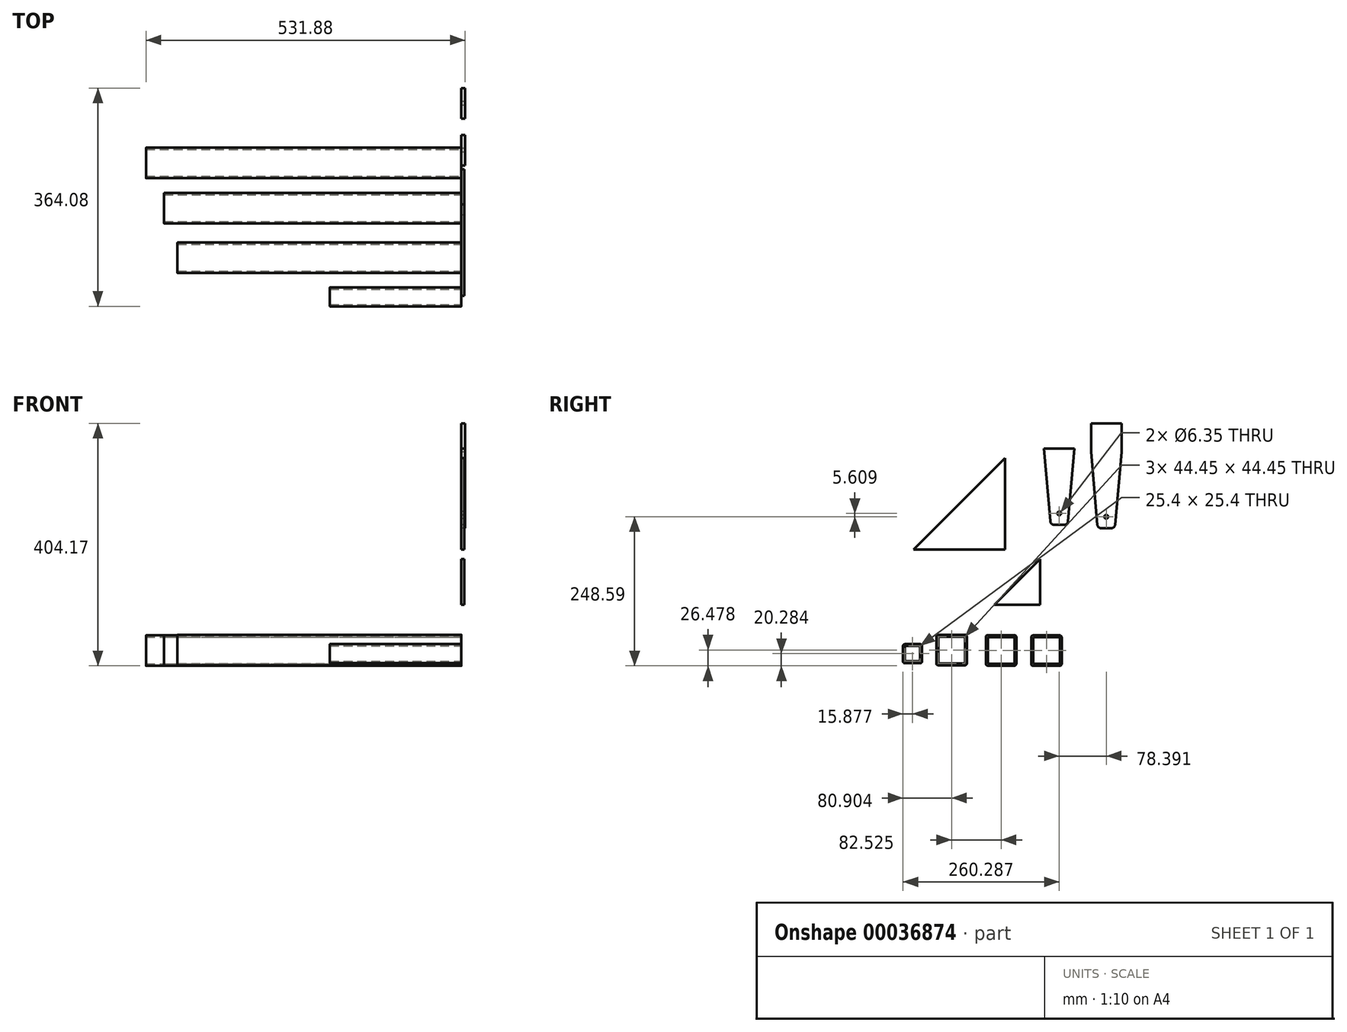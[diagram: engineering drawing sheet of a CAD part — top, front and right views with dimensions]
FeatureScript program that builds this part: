
annotation { "Feature Type Name" : "Feature", "Feature Type Description" : "" }
export const myFeature = defineFeature(function(context is Context, id is Id, definition is map)
    precondition{}
    {
        {
            var Q0;
            Q0=qCreatedBy(makeId("Right.planeOp"),FACE);
            var sketch = newSketch(context, id + "F0", { "sketchPlane" : qUnion([Q0])});
            skLineSegment(sketch, "E0.rect.bottom", {"start": v(22.23, 25.4) * mm, "end": v(-22.23, 25.4) * mm});
            skLineSegment(sketch, "E0.rect.top", {"start": v(22.23, -25.4) * mm, "end": v(-22.23, -25.4) * mm});
            skLineSegment(sketch, "E0.rect.left", {"start": v(25.4, 22.22) * mm, "end": v(25.4, -22.23) * mm});
            skLineSegment(sketch, "E0.rect.right", {"start": v(-25.4, 22.23) * mm, "end": v(-25.4, -22.22) * mm});
            skPoint(sketch, "E0.rect.middle", {"position": v(0, 0) * mm});
            skPoint(sketch, "E1.visualSharp", {"position": v(-25.4, 25.4) * mm});
            skArc(sketch, "E1.filletArc", {"start": v(-22.23, 25.4) * mm, "mid": v(-24.47, 24.47) * mm, "end": v(-25.4, 22.23) * mm});
            skPoint(sketch, "E2.visualSharp", {"position": v(25.4, 25.4) * mm});
            skArc(sketch, "E2.filletArc", {"start": v(25.4, 22.22) * mm, "mid": v(24.47, 24.47) * mm, "end": v(22.23, 25.4) * mm});
            skPoint(sketch, "E3.visualSharp", {"position": v(25.4, -25.4) * mm});
            skArc(sketch, "E3.filletArc", {"start": v(22.23, -25.4) * mm, "mid": v(24.47, -24.47) * mm, "end": v(25.4, -22.23) * mm});
            skPoint(sketch, "E4.visualSharp", {"position": v(-25.4, -25.4) * mm});
            skArc(sketch, "E4.filletArc", {"start": v(-25.4, -22.22) * mm, "mid": v(-24.47, -24.47) * mm, "end": v(-22.23, -25.4) * mm});
            skLineSegment(sketch, "E5.bottom", {"start": v(-22.23, 22.23) * mm, "end": v(22.22, 22.23) * mm});
            skLineSegment(sketch, "E5.top", {"start": v(-22.23, -22.23) * mm, "end": v(22.22, -22.23) * mm});
            skLineSegment(sketch, "E5.left", {"start": v(-22.23, 22.23) * mm, "end": v(-22.23, -22.23) * mm});
            skLineSegment(sketch, "E5.right", {"start": v(22.22, 22.23) * mm, "end": v(22.22, -22.23) * mm});
            skSolve(sketch);
        }
        {
            var Q0;
            Q0=qCreatedBy(makeId("Right.planeOp"),FACE);
            var sketch = newSketch(context, id + "F1", { "sketchPlane" : qUnion([Q0])});
            skLineSegment(sketch, "E6.rect.bottom", {"start": v(-61.4, 48.87) * mm, "end": v(-105.85, 48.87) * mm});
            skLineSegment(sketch, "E6.rect.top", {"start": v(-61.4, -1.93) * mm, "end": v(-105.85, -1.93) * mm});
            skLineSegment(sketch, "E6.rect.left", {"start": v(-58.23, 45.7) * mm, "end": v(-58.23, 1.24) * mm});
            skLineSegment(sketch, "E6.rect.right", {"start": v(-109.03, 45.7) * mm, "end": v(-109.03, 1.24) * mm});
            skPoint(sketch, "E6.rect.middle", {"position": v(-83.63, 23.47) * mm});
            skPoint(sketch, "E7.visualSharp", {"position": v(-109.03, 48.87) * mm});
            skArc(sketch, "E7.filletArc", {"start": v(-105.85, 48.87) * mm, "mid": v(-108.1, 47.94) * mm, "end": v(-109.03, 45.7) * mm});
            skPoint(sketch, "E8.visualSharp", {"position": v(-58.23, 48.87) * mm});
            skArc(sketch, "E8.filletArc", {"start": v(-58.23, 45.7) * mm, "mid": v(-59.16, 47.94) * mm, "end": v(-61.4, 48.87) * mm});
            skPoint(sketch, "E9.visualSharp", {"position": v(-58.23, -1.93) * mm});
            skArc(sketch, "E9.filletArc", {"start": v(-61.4, -1.93) * mm, "mid": v(-59.16, -1) * mm, "end": v(-58.23, 1.24) * mm});
            skPoint(sketch, "E10.visualSharp", {"position": v(-109.03, -1.93) * mm});
            skArc(sketch, "E10.filletArc", {"start": v(-109.03, 1.24) * mm, "mid": v(-108.1, -1) * mm, "end": v(-105.85, -1.93) * mm});
            skLineSegment(sketch, "E11.bottom", {"start": v(-105.85, 45.7) * mm, "end": v(-61.4, 45.7) * mm});
            skLineSegment(sketch, "E11.top", {"start": v(-105.85, 1.24) * mm, "end": v(-61.4, 1.24) * mm});
            skLineSegment(sketch, "E11.left", {"start": v(-105.85, 45.7) * mm, "end": v(-105.85, 1.24) * mm});
            skLineSegment(sketch, "E11.right", {"start": v(-61.4, 45.7) * mm, "end": v(-61.4, 1.24) * mm});
            skSolve(sketch);
        }
        {
            var Q0;
            Q0=qCreatedBy(makeId("Right.planeOp"),FACE);
            var sketch = newSketch(context, id + "F2", { "sketchPlane" : qUnion([Q0])});
            skLineSegment(sketch, "E12.rect.bottom", {"start": v(70.63, 77.05) * mm, "end": v(26.18, 77.05) * mm});
            skLineSegment(sketch, "E12.rect.top", {"start": v(70.63, 26.25) * mm, "end": v(26.18, 26.25) * mm});
            skLineSegment(sketch, "E12.rect.left", {"start": v(73.8, 73.88) * mm, "end": v(73.8, 29.43) * mm});
            skLineSegment(sketch, "E12.rect.right", {"start": v(23, 73.88) * mm, "end": v(23, 29.43) * mm});
            skPoint(sketch, "E12.rect.middle", {"position": v(48.4, 51.65) * mm});
            skPoint(sketch, "E13.visualSharp", {"position": v(23, 77.05) * mm});
            skArc(sketch, "E13.filletArc", {"start": v(26.18, 77.05) * mm, "mid": v(23.94, 76.12) * mm, "end": v(23, 73.88) * mm});
            skPoint(sketch, "E14.visualSharp", {"position": v(73.8, 77.05) * mm});
            skArc(sketch, "E14.filletArc", {"start": v(73.8, 73.88) * mm, "mid": v(72.88, 76.12) * mm, "end": v(70.63, 77.05) * mm});
            skPoint(sketch, "E15.visualSharp", {"position": v(73.8, 26.25) * mm});
            skArc(sketch, "E15.filletArc", {"start": v(70.63, 26.25) * mm, "mid": v(72.88, 27.18) * mm, "end": v(73.8, 29.43) * mm});
            skPoint(sketch, "E16.visualSharp", {"position": v(23, 26.25) * mm});
            skArc(sketch, "E16.filletArc", {"start": v(23, 29.43) * mm, "mid": v(23.94, 27.18) * mm, "end": v(26.18, 26.25) * mm});
            skLineSegment(sketch, "E17", {"start": v(26.18, 73.88) * mm, "end": v(70.63, 73.88) * mm});
            skLineSegment(sketch, "E18", {"start": v(70.63, 29.43) * mm, "end": v(70.63, 73.88) * mm});
            skLineSegment(sketch, "E19", {"start": v(70.63, 29.43) * mm, "end": v(26.18, 29.43) * mm});
            skLineSegment(sketch, "E20", {"start": v(26.18, 29.43) * mm, "end": v(26.18, 73.88) * mm});
            skSolve(sketch);
        }
        {
            var Q0;
            Q0=qCreatedBy(makeId("Right.planeOp"),FACE);
            var sketch = newSketch(context, id + "F3", { "sketchPlane" : qUnion([Q0])});
            skLineSegment(sketch, "E21.rect.bottom", {"start": v(-34.94, -109.2) * mm, "end": v(-60.34, -109.2) * mm});
            skLineSegment(sketch, "E21.rect.top", {"start": v(-34.94, -77.46) * mm, "end": v(-60.34, -77.46) * mm});
            skLineSegment(sketch, "E21.rect.left", {"start": v(-31.76, -106.03) * mm, "end": v(-31.76, -80.63) * mm});
            skLineSegment(sketch, "E21.rect.right", {"start": v(-63.51, -106.03) * mm, "end": v(-63.51, -80.63) * mm});
            skPoint(sketch, "E21.rect.middle", {"position": v(-47.64, -93.33) * mm});
            skPoint(sketch, "E22.visualSharp", {"position": v(-31.76, -77.46) * mm});
            skArc(sketch, "E22.filletArc", {"start": v(-31.76, -80.63) * mm, "mid": v(-32.7, -78.39) * mm, "end": v(-34.94, -77.46) * mm});
            skPoint(sketch, "E23.visualSharp", {"position": v(-63.51, -77.46) * mm});
            skArc(sketch, "E23.filletArc", {"start": v(-60.34, -77.46) * mm, "mid": v(-62.58, -78.39) * mm, "end": v(-63.51, -80.63) * mm});
            skPoint(sketch, "E24.visualSharp", {"position": v(-63.51, -109.2) * mm});
            skArc(sketch, "E24.filletArc", {"start": v(-63.51, -106.03) * mm, "mid": v(-62.58, -108.28) * mm, "end": v(-60.34, -109.2) * mm});
            skPoint(sketch, "E25.visualSharp", {"position": v(-31.76, -109.2) * mm});
            skArc(sketch, "E25.filletArc", {"start": v(-34.94, -109.2) * mm, "mid": v(-32.7, -108.28) * mm, "end": v(-31.76, -106.03) * mm});
            skLineSegment(sketch, "E26.bottom", {"start": v(-60.34, -80.63) * mm, "end": v(-34.94, -80.63) * mm});
            skLineSegment(sketch, "E26.top", {"start": v(-60.34, -106.03) * mm, "end": v(-34.94, -106.03) * mm});
            skLineSegment(sketch, "E26.left", {"start": v(-60.34, -80.63) * mm, "end": v(-60.34, -106.03) * mm});
            skLineSegment(sketch, "E26.right", {"start": v(-34.94, -80.63) * mm, "end": v(-34.94, -106.03) * mm});
            skSolve(sketch);
        }
        {
            var Q0;
            Q0 = qSketchRegion(id + "F2", true);
            extrude(context, id + "F4", {"entities" : qUnion([Q0]), "oppositeDirection" : true, "depth" : 525.53 * mm});
        }
        {
            var Q0;
            Q0 = qSketchRegion(id + "F0", true);
            extrude(context, id + "F5", {"entities" : qUnion([Q0]), "oppositeDirection" : true, "depth" : 495.3 * mm});
        }
        {
            var Q0;
            Q0 = qSketchRegion(id + "F1", true);
            extrude(context, id + "F6", {"entities" : qUnion([Q0]), "oppositeDirection" : true, "depth" : 472.95 * mm});
        }
        {
            var Q0;
            Q0=makeQuery(id+"F4.opExtrude","SWEPT_BODY",BODY,{"disambiguationData":[OSD([sQuery(id+"F2.wireOp",EDGE,"E12.rect.bottom"),sQuery(id+"F2.wireOp",EDGE,"E12.rect.top"),sQuery(id+"F2.wireOp",EDGE,"E12.rect.left"),sQuery(id+"F2.wireOp",EDGE,"E12.rect.right"),sQuery(id+"F2.wireOp",EDGE,"E13.filletArc"),sQuery(id+"F2.wireOp",EDGE,"E14.filletArc"),sQuery(id+"F2.wireOp",EDGE,"E15.filletArc"),sQuery(id+"F2.wireOp",EDGE,"E16.filletArc"),sQuery(id+"F2.wireOp",EDGE,"E17"),sQuery(id+"F2.wireOp",EDGE,"E18"),sQuery(id+"F2.wireOp",EDGE,"E19"),sQuery(id+"F2.wireOp",EDGE,"E20")])]});
            transform(context, id + "F7", {"entities" : qUnion([Q0]), "transformType" : TransformType.TRANSLATION_3D, "dx" : 0 * mm, "dy" : 0 * mm, "dz" : 54.67 * mm, "makeCopy" : false});
        }
        {
            var Q0;
            Q0=makeQuery(id+"F6.opExtrude","SWEPT_BODY",BODY,{"disambiguationData":[OSD([sQuery(id+"F1.wireOp",EDGE,"E6.rect.bottom"),sQuery(id+"F1.wireOp",EDGE,"E6.rect.top"),sQuery(id+"F1.wireOp",EDGE,"E6.rect.left"),sQuery(id+"F1.wireOp",EDGE,"E6.rect.right"),sQuery(id+"F1.wireOp",EDGE,"E7.filletArc"),sQuery(id+"F1.wireOp",EDGE,"E8.filletArc"),sQuery(id+"F1.wireOp",EDGE,"E9.filletArc"),sQuery(id+"F1.wireOp",EDGE,"E10.filletArc"),sQuery(id+"F1.wireOp",EDGE,"E11.bottom"),sQuery(id+"F1.wireOp",EDGE,"E11.top"),sQuery(id+"F1.wireOp",EDGE,"E11.left"),sQuery(id+"F1.wireOp",EDGE,"E11.right")])]});
            transform(context, id + "F8", {"entities" : qUnion([Q0]), "transformType" : TransformType.TRANSLATION_3D, "dx" : 0 * mm, "dy" : -96.27 * mm, "dz" : 0 * mm, "makeCopy" : false});
        }
        {
            var Q0;
            Q0 = qSketchRegion(id + "F3", true);
            extrude(context, id + "F9", {"entities" : qUnion([Q0]), "oppositeDirection" : true, "depth" : 219.2 * mm});
        }
        {
            var Q0;
            Q0=makeQuery(id+"F4.opExtrude","SWEPT_BODY",BODY,{"disambiguationData":[OSD([sQuery(id+"F2.wireOp",EDGE,"E12.rect.bottom"),sQuery(id+"F2.wireOp",EDGE,"E12.rect.top"),sQuery(id+"F2.wireOp",EDGE,"E12.rect.left"),sQuery(id+"F2.wireOp",EDGE,"E12.rect.right"),sQuery(id+"F2.wireOp",EDGE,"E13.filletArc"),sQuery(id+"F2.wireOp",EDGE,"E14.filletArc"),sQuery(id+"F2.wireOp",EDGE,"E15.filletArc"),sQuery(id+"F2.wireOp",EDGE,"E16.filletArc"),sQuery(id+"F2.wireOp",EDGE,"E17"),sQuery(id+"F2.wireOp",EDGE,"E18"),sQuery(id+"F2.wireOp",EDGE,"E19"),sQuery(id+"F2.wireOp",EDGE,"E20")])]});
            transform(context, id + "F10", {"entities" : qUnion([Q0]), "transformType" : TransformType.TRANSLATION_3D, "dx" : 0 * mm, "dy" : 40.4 * mm, "dz" : -107.47 * mm, "makeCopy" : false});
        }
        {
            var Q0;
            Q0=makeQuery(id+"F6.opExtrude","SWEPT_BODY",BODY,{"disambiguationData":[OSD([sQuery(id+"F1.wireOp",EDGE,"E6.rect.bottom"),sQuery(id+"F1.wireOp",EDGE,"E6.rect.top"),sQuery(id+"F1.wireOp",EDGE,"E6.rect.left"),sQuery(id+"F1.wireOp",EDGE,"E6.rect.right"),sQuery(id+"F1.wireOp",EDGE,"E7.filletArc"),sQuery(id+"F1.wireOp",EDGE,"E8.filletArc"),sQuery(id+"F1.wireOp",EDGE,"E9.filletArc"),sQuery(id+"F1.wireOp",EDGE,"E10.filletArc"),sQuery(id+"F1.wireOp",EDGE,"E11.bottom"),sQuery(id+"F1.wireOp",EDGE,"E11.top"),sQuery(id+"F1.wireOp",EDGE,"E11.left"),sQuery(id+"F1.wireOp",EDGE,"E11.right")])]});
            transform(context, id + "F11", {"entities" : qUnion([Q0]), "transformType" : TransformType.TRANSLATION_3D, "dx" : 0 * mm, "dy" : 110.6 * mm, "dz" : -23.53 * mm, "makeCopy" : false});
        }
        {
            var Q0;
            Q0=makeQuery(id+"F9.opExtrude","SWEPT_BODY",BODY,{"disambiguationData":[OSD([sQuery(id+"F3.wireOp",EDGE,"E21.rect.bottom"),sQuery(id+"F3.wireOp",EDGE,"E21.rect.top"),sQuery(id+"F3.wireOp",EDGE,"E21.rect.left"),sQuery(id+"F3.wireOp",EDGE,"E21.rect.right"),sQuery(id+"F3.wireOp",EDGE,"E22.filletArc"),sQuery(id+"F3.wireOp",EDGE,"E23.filletArc"),sQuery(id+"F3.wireOp",EDGE,"E24.filletArc"),sQuery(id+"F3.wireOp",EDGE,"E25.filletArc"),sQuery(id+"F3.wireOp",EDGE,"E26.bottom"),sQuery(id+"F3.wireOp",EDGE,"E26.top"),sQuery(id+"F3.wireOp",EDGE,"E26.left"),sQuery(id+"F3.wireOp",EDGE,"E26.right")])]});
            transform(context, id + "F12", {"entities" : qUnion([Q0]), "transformType" : TransformType.TRANSLATION_3D, "dx" : 0 * mm, "dy" : -86.68 * mm, "dz" : 87.07 * mm, "makeCopy" : false});
        }
        {
            var Q0;
            Q0=qCreatedBy(makeId("Right.planeOp"),FACE);
            var sketch = newSketch(context, id + "F13", { "sketchPlane" : qUnion([Q0])});
            skLineSegment(sketch, "E27", {"start": v(25.4, 39.69) * mm, "end": v(14.8, -81.52) * mm});
            skArc(sketch, "E28", {"start": v(14.8, -81.52) * mm, "mid": v(12.76, -85.64) * mm, "end": v(8.47, -87.31) * mm});
            skLineSegment(sketch, "E29", {"start": v(8.47, -87.31) * mm, "end": v(-8.47, -87.31) * mm});
            skArc(sketch, "E30", {"start": v(-8.47, -87.31) * mm, "mid": v(-12.76, -85.64) * mm, "end": v(-14.8, -81.52) * mm});
            skLineSegment(sketch, "E31", {"start": v(-14.8, -81.52) * mm, "end": v(-25.4, 39.69) * mm});
            skLineSegment(sketch, "E32", {"start": v(25.4, 39.69) * mm, "end": v(25.4, 87.31) * mm});
            skLineSegment(sketch, "E33", {"start": v(25.4, 87.31) * mm, "end": v(-25.4, 87.31) * mm});
            skLineSegment(sketch, "E34", {"start": v(-25.4, 87.31) * mm, "end": v(-25.4, 39.69) * mm});
            skCircle(sketch, "E35", {"center": v(0, -68.26) * mm, "radius": 3.18 * mm});
            skSolve(sketch);
        }
        {
            var Q0;
            Q0=makeQuery(id+"F5.opExtrude","SWEPT_BODY",BODY,{"disambiguationData":[OSD([sQuery(id+"F0.wireOp",EDGE,"E0.rect.bottom"),sQuery(id+"F0.wireOp",EDGE,"E0.rect.top"),sQuery(id+"F0.wireOp",EDGE,"E0.rect.left"),sQuery(id+"F0.wireOp",EDGE,"E0.rect.right"),sQuery(id+"F0.wireOp",EDGE,"E1.filletArc"),sQuery(id+"F0.wireOp",EDGE,"E2.filletArc"),sQuery(id+"F0.wireOp",EDGE,"E3.filletArc"),sQuery(id+"F0.wireOp",EDGE,"E4.filletArc"),sQuery(id+"F0.wireOp",EDGE,"E5.bottom"),sQuery(id+"F0.wireOp",EDGE,"E5.top"),sQuery(id+"F0.wireOp",EDGE,"E5.left"),sQuery(id+"F0.wireOp",EDGE,"E5.right")])]});
            transform(context, id + "F14", {"entities" : qUnion([Q0]), "transformType" : TransformType.TRANSLATION_3D, "dx" : 0 * mm, "dy" : 28.29 * mm, "dz" : -254.67 * mm, "makeCopy" : false});
        }
        {
            var Q0;
            Q0 = qSketchRegion(id + "F13", true);
            extrude(context, id + "F15", {"entities" : qUnion([Q0]), "depth" : 6.35 * mm});
        }
        {
            var Q0;
            Q0=makeQuery(id+"F15.opExtrude","SWEPT_BODY",BODY,{"disambiguationData":[OSD([sQuery(id+"F13.wireOp",EDGE,"E27"),sQuery(id+"F13.wireOp",EDGE,"E28"),sQuery(id+"F13.wireOp",EDGE,"E29"),sQuery(id+"F13.wireOp",EDGE,"E30"),sQuery(id+"F13.wireOp",EDGE,"E31"),sQuery(id+"F13.wireOp",EDGE,"E32"),sQuery(id+"F13.wireOp",EDGE,"E33"),sQuery(id+"F13.wireOp",EDGE,"E34"),sQuery(id+"F13.wireOp",EDGE,"E35")])]});
            transform(context, id + "F16", {"entities" : qUnion([Q0]), "transformType" : TransformType.TRANSLATION_3D, "dx" : 0 * mm, "dy" : 203.54 * mm, "dz" : 36.31 * mm, "makeCopy" : false});
        }
        {
            var Q0;
            Q0=makeQuery(id+"F9.opExtrude","SWEPT_BODY",BODY,{"disambiguationData":[OSD([sQuery(id+"F3.wireOp",EDGE,"E21.rect.bottom"),sQuery(id+"F3.wireOp",EDGE,"E21.rect.top"),sQuery(id+"F3.wireOp",EDGE,"E21.rect.left"),sQuery(id+"F3.wireOp",EDGE,"E21.rect.right"),sQuery(id+"F3.wireOp",EDGE,"E22.filletArc"),sQuery(id+"F3.wireOp",EDGE,"E23.filletArc"),sQuery(id+"F3.wireOp",EDGE,"E24.filletArc"),sQuery(id+"F3.wireOp",EDGE,"E25.filletArc"),sQuery(id+"F3.wireOp",EDGE,"E26.bottom"),sQuery(id+"F3.wireOp",EDGE,"E26.top"),sQuery(id+"F3.wireOp",EDGE,"E26.left"),sQuery(id+"F3.wireOp",EDGE,"E26.right")])]});
            var Q1;
            Q1=makeQuery(id+"F6.opExtrude","SWEPT_BODY",BODY,{"disambiguationData":[OSD([sQuery(id+"F1.wireOp",EDGE,"E6.rect.bottom"),sQuery(id+"F1.wireOp",EDGE,"E6.rect.top"),sQuery(id+"F1.wireOp",EDGE,"E6.rect.left"),sQuery(id+"F1.wireOp",EDGE,"E6.rect.right"),sQuery(id+"F1.wireOp",EDGE,"E7.filletArc"),sQuery(id+"F1.wireOp",EDGE,"E8.filletArc"),sQuery(id+"F1.wireOp",EDGE,"E9.filletArc"),sQuery(id+"F1.wireOp",EDGE,"E10.filletArc"),sQuery(id+"F1.wireOp",EDGE,"E11.bottom"),sQuery(id+"F1.wireOp",EDGE,"E11.top"),sQuery(id+"F1.wireOp",EDGE,"E11.left"),sQuery(id+"F1.wireOp",EDGE,"E11.right")])]});
            var Q2;
            Q2=makeQuery(id+"F4.opExtrude","SWEPT_BODY",BODY,{"disambiguationData":[OSD([sQuery(id+"F2.wireOp",EDGE,"E12.rect.bottom"),sQuery(id+"F2.wireOp",EDGE,"E12.rect.top"),sQuery(id+"F2.wireOp",EDGE,"E12.rect.left"),sQuery(id+"F2.wireOp",EDGE,"E12.rect.right"),sQuery(id+"F2.wireOp",EDGE,"E13.filletArc"),sQuery(id+"F2.wireOp",EDGE,"E14.filletArc"),sQuery(id+"F2.wireOp",EDGE,"E15.filletArc"),sQuery(id+"F2.wireOp",EDGE,"E16.filletArc"),sQuery(id+"F2.wireOp",EDGE,"E17"),sQuery(id+"F2.wireOp",EDGE,"E18"),sQuery(id+"F2.wireOp",EDGE,"E19"),sQuery(id+"F2.wireOp",EDGE,"E20")])]});
            transform(context, id + "F17", {"entities" : qUnion([Q0, Q1, Q2]), "transformType" : TransformType.TRANSLATION_3D, "dx" : 0 * mm, "dy" : 15.06 * mm, "dz" : -254 * mm, "makeCopy" : false});
        }
        {
            var Q0;
            Q0=qCreatedBy(makeId("Right.planeOp"),FACE);
            var sketch = newSketch(context, id + "F18", { "sketchPlane" : qUnion([Q0])});
            skLineSegment(sketch, "E36", {"start": v(25.4, 63.5) * mm, "end": v(14.8, -57.7) * mm});
            skArc(sketch, "E37", {"start": v(14.8, -57.7) * mm, "mid": v(12.76, -61.83) * mm, "end": v(8.47, -63.5) * mm});
            skLineSegment(sketch, "E38", {"start": v(8.47, -63.5) * mm, "end": v(-8.47, -63.5) * mm});
            skArc(sketch, "E39", {"start": v(-8.47, -63.5) * mm, "mid": v(-12.76, -61.83) * mm, "end": v(-14.8, -57.7) * mm});
            skLineSegment(sketch, "E40", {"start": v(-14.8, -57.7) * mm, "end": v(-14.84, -57.17) * mm});
            skLineSegment(sketch, "E41", {"start": v(-25.4, 63.5) * mm, "end": v(25.4, 63.5) * mm});
            skLineSegment(sketch, "E42", {"start": v(-25.4, 63.5) * mm, "end": v(-14.84, -57.17) * mm});
            skCircle(sketch, "E43", {"center": v(0, -44.45) * mm, "radius": 3.18 * mm});
            skSolve(sketch);
        }
        {
            var Q0;
            Q0=makeQuery(id+"F18.imprint","IMPRINT",FACE,{"disambiguationData":[TD([[makeQuery(id+"F18.imprint","IMPRINT",EDGE,{"derivedFrom":sQuery(id+"F18.wireOp",EDGE,"E36")}),-1.0]])]});
            extrude(context, id + "F19", {"entities" : qUnion([Q0]), "depth" : 6.35 * mm});
        }
        {
            var Q0;
            Q0=makeQuery(id+"F19.opExtrude","SWEPT_BODY",BODY,{"disambiguationData":[OSD([sQuery(id+"F18.wireOp",EDGE,"E36"),sQuery(id+"F18.wireOp",EDGE,"E37"),sQuery(id+"F18.wireOp",EDGE,"E38"),sQuery(id+"F18.wireOp",EDGE,"E39"),sQuery(id+"F18.wireOp",EDGE,"E40"),sQuery(id+"F18.wireOp",EDGE,"E41"),sQuery(id+"F18.wireOp",EDGE,"E42"),sQuery(id+"F18.wireOp",EDGE,"E43")])]});
            transform(context, id + "F20", {"entities" : qUnion([Q0]), "transformType" : TransformType.TRANSLATION_3D, "dx" : 0 * mm, "dy" : 125.15 * mm, "dz" : 18.1 * mm, "makeCopy" : false});
        }
        {
            var Q0;
            Q0=qCreatedBy(makeId("Right.planeOp"),FACE);
            var sketch = newSketch(context, id + "F21", { "sketchPlane" : qUnion([Q0])});
            skLineSegment(sketch, "E44", {"start": v(-59.42, -38.6) * mm, "end": v(16.78, -38.6) * mm});
            skLineSegment(sketch, "E45", {"start": v(16.78, -38.6) * mm, "end": v(16.78, 37.6) * mm});
            skLineSegment(sketch, "E46", {"start": v(16.78, 37.6) * mm, "end": v(-59.42, -38.6) * mm});
            skSolve(sketch);
        }
        {
            var Q0;
            Q0=makeQuery(id+"F21.imprint","IMPRINT",FACE,{"disambiguationData":[TD([[makeQuery(id+"F21.imprint","IMPRINT",EDGE,{"derivedFrom":sQuery(id+"F21.wireOp",EDGE,"E44")}),1.0]])]});
            extrude(context, id + "F22", {"entities" : qUnion([Q0]), "depth" : 4.78 * mm});
        }
        {
            var Q0;
            Q0=makeQuery(id+"F22.opExtrude","SWEPT_BODY",BODY,{"disambiguationData":[OSD([sQuery(id+"F21.wireOp",EDGE,"E44"),sQuery(id+"F21.wireOp",EDGE,"E45"),sQuery(id+"F21.wireOp",EDGE,"E46")])]});
            transform(context, id + "F23", {"entities" : qUnion([Q0]), "transformType" : TransformType.TRANSLATION_3D, "dx" : 0 * mm, "dy" : 76.68 * mm, "dz" : -140.1 * mm, "makeCopy" : false});
        }
        {
            var Q0;
            Q0=qCreatedBy(makeId("Right.planeOp"),FACE);
            var sketch = newSketch(context, id + "F24", { "sketchPlane" : qUnion([Q0])});
            skLineSegment(sketch, "E47", {"start": v(35.14, 65.84) * mm, "end": v(35.14, -86.56) * mm});
            skLineSegment(sketch, "E48", {"start": v(35.14, -86.56) * mm, "end": v(-117.26, -86.56) * mm});
            skLineSegment(sketch, "E49", {"start": v(-117.26, -86.56) * mm, "end": v(35.14, 65.84) * mm});
            skSolve(sketch);
        }
        {
            var Q0;
            Q0=makeQuery(id+"F24.imprint","IMPRINT",FACE,{"disambiguationData":[TD([[makeQuery(id+"F24.imprint","IMPRINT",EDGE,{"derivedFrom":sQuery(id+"F24.wireOp",EDGE,"E47")}),-1.0]])]});
            extrude(context, id + "F25", {"entities" : qUnion([Q0]), "depth" : 4.78 * mm});
        }
    });
